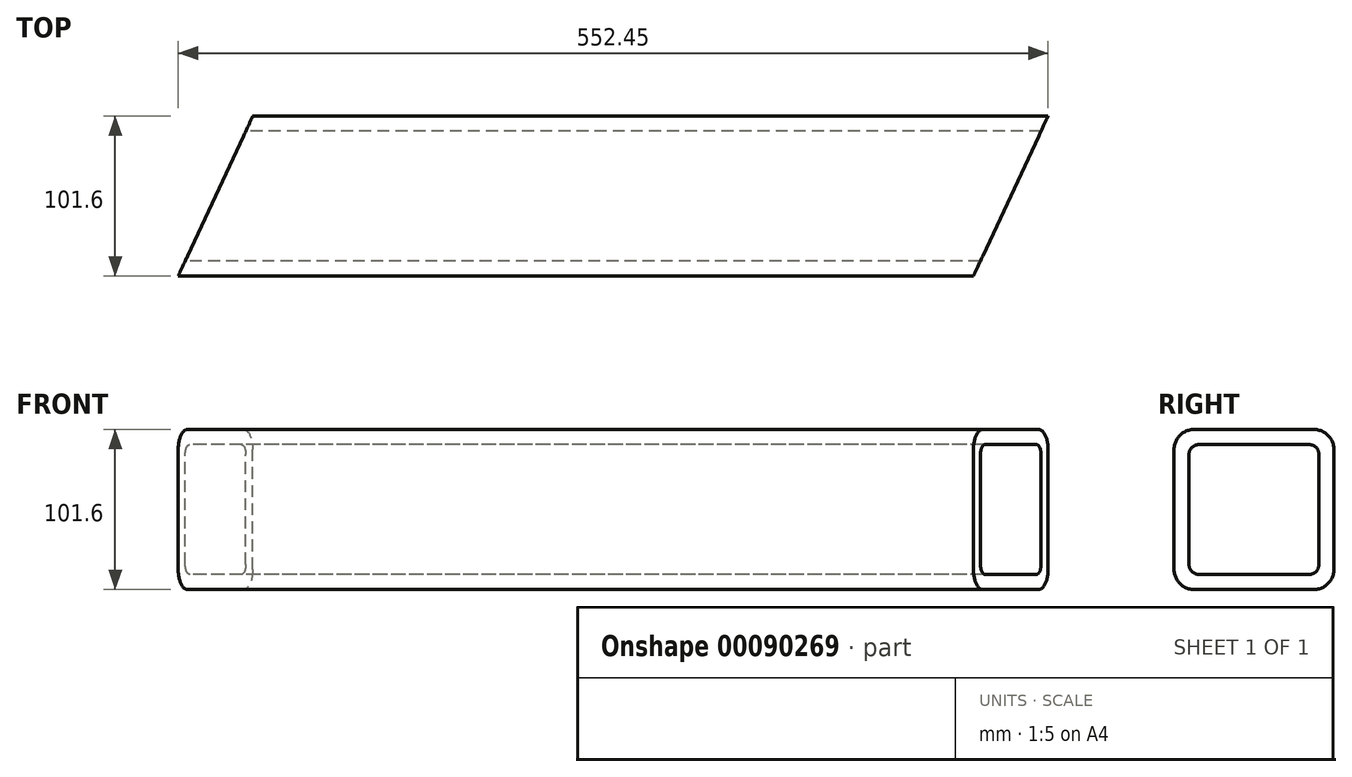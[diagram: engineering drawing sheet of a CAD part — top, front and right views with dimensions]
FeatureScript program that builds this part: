
annotation { "Feature Type Name" : "Feature", "Feature Type Description" : "" }
export const myFeature = defineFeature(function(context is Context, id is Id, definition is map)
    precondition{}
    {
        {
            var Q0;
            Q0=qCreatedBy(makeId("Right.planeOp"),FACE);
            var sketch = newSketch(context, id + "F0", { "sketchPlane" : qUnion([Q0])});
            skLineSegment(sketch, "E0.bottom", {"start": v(12.7, 0) * mm, "end": v(88.9, 0) * mm});
            skLineSegment(sketch, "E0.top", {"start": v(12.7, -101.6) * mm, "end": v(88.9, -101.6) * mm});
            skLineSegment(sketch, "E0.left", {"start": v(0, -12.7) * mm, "end": v(0, -88.9) * mm});
            skLineSegment(sketch, "E0.right", {"start": v(101.6, -12.7) * mm, "end": v(101.6, -88.9) * mm});
            skLineSegment(sketch, "E1.0", {"start": v(15.88, -9.53) * mm, "end": v(85.73, -9.53) * mm});
            skLineSegment(sketch, "E1.1", {"start": v(9.53, -15.88) * mm, "end": v(9.53, -85.73) * mm});
            skLineSegment(sketch, "E1.2", {"start": v(15.88, -92.08) * mm, "end": v(85.73, -92.08) * mm});
            skLineSegment(sketch, "E1.3", {"start": v(92.08, -15.88) * mm, "end": v(92.08, -85.73) * mm});
            skPoint(sketch, "E2.visualSharp", {"position": v(0, 0) * mm});
            skArc(sketch, "E2.filletArc", {"start": v(12.7, 0) * mm, "mid": v(3.72, -3.72) * mm, "end": v(0, -12.7) * mm});
            skPoint(sketch, "E3.visualSharp", {"position": v(101.6, 0) * mm});
            skArc(sketch, "E3.filletArc", {"start": v(101.6, -12.7) * mm, "mid": v(97.88, -3.72) * mm, "end": v(88.9, 0) * mm});
            skPoint(sketch, "E4.visualSharp", {"position": v(101.6, -101.6) * mm});
            skArc(sketch, "E4.filletArc", {"start": v(88.9, -101.6) * mm, "mid": v(97.88, -97.88) * mm, "end": v(101.6, -88.9) * mm});
            skPoint(sketch, "E5.visualSharp", {"position": v(0, -101.6) * mm});
            skArc(sketch, "E5.filletArc", {"start": v(0, -88.9) * mm, "mid": v(3.72, -97.88) * mm, "end": v(12.7, -101.6) * mm});
            skPoint(sketch, "E6.visualSharp", {"position": v(9.53, -92.08) * mm});
            skArc(sketch, "E6.filletArc", {"start": v(9.53, -85.73) * mm, "mid": v(11.38, -90.22) * mm, "end": v(15.88, -92.08) * mm});
            skPoint(sketch, "E7.visualSharp", {"position": v(92.08, -92.08) * mm});
            skArc(sketch, "E7.filletArc", {"start": v(85.73, -92.08) * mm, "mid": v(90.22, -90.22) * mm, "end": v(92.08, -85.73) * mm});
            skPoint(sketch, "E8.visualSharp", {"position": v(92.08, -9.53) * mm});
            skArc(sketch, "E8.filletArc", {"start": v(92.08, -15.88) * mm, "mid": v(90.22, -11.38) * mm, "end": v(85.73, -9.52) * mm});
            skPoint(sketch, "E9.visualSharp", {"position": v(9.53, -9.53) * mm});
            skArc(sketch, "E9.filletArc", {"start": v(15.88, -9.53) * mm, "mid": v(11.38, -11.38) * mm, "end": v(9.53, -15.88) * mm});
            skSolve(sketch);
        }
        {
            var Q0;
            Q0=makeQuery(id+"F0.imprint","IMPRINT",FACE,{"disambiguationData":[TD([[makeQuery(id+"F0.imprint","IMPRINT",EDGE,{"derivedFrom":sQuery(id+"F0.wireOp",EDGE,"E0.bottom")}),-1.0]])]});
            extrude(context, id + "F1", {"entities" : qUnion([Q0]), "depth" : 1651 * mm});
        }
        {
            var Q0;
            Q0=qCreatedBy(makeId("Top.planeOp"),FACE);
            var sketch = newSketch(context, id + "F2", { "sketchPlane" : qUnion([Q0])});
            skLineSegment(sketch, "E10.0", {"start": v(1651, 0) * mm, "end": v(0, 0) * mm});
            skLineSegment(sketch, "E10.1", {"start": v(1651, 101.6) * mm, "end": v(0, 101.6) * mm});
            skLineSegment(sketch, "E11", {"start": v(47.38, 101.6) * mm, "end": v(0, 0) * mm});
            skLineSegment(sketch, "E12", {"start": v(505.07, 0) * mm, "end": v(552.45, 101.6) * mm});
            skLineSegment(sketch, "E13.0", {"start": v(0, 12.7) * mm, "end": v(0, 88.9) * mm});
            skLineSegment(sketch, "E14.0", {"start": v(0, 101.6) * mm, "end": v(0, 88.9) * mm});
            skLineSegment(sketch, "E15.0", {"start": v(0, 12.7) * mm, "end": v(0, 0) * mm});
            skLineSegment(sketch, "E16.0", {"start": v(1651, 12.7) * mm, "end": v(1651, 88.9) * mm});
            skLineSegment(sketch, "E17.0", {"start": v(1651, 101.6) * mm, "end": v(1651, 88.9) * mm});
            skLineSegment(sketch, "E18.0", {"start": v(1651, 12.7) * mm, "end": v(1651, 0) * mm});
            skSolve(sketch);
        }
        {
            var Q0;
            {var subQ0=sQuery(id+"F2.wireOp",EDGE,"E12");Q0=makeQuery(id+"F2.imprint","IMPRINT",FACE,{"disambiguationData":[TD([[makeQuery(id+"F2.imprint","IMPRINT",EDGE,{"derivedFrom":subQ0}),-1.0]])]});}
            var Q1;
            {var subQ1=sQuery(id+"F2.wireOp",EDGE,"E11");Q1=makeQuery(id+"F2.imprint","IMPRINT",FACE,{"disambiguationData":[TD([[makeQuery(id+"F2.imprint","IMPRINT",EDGE,{"derivedFrom":subQ1}),-1.0]])]});}
            extrude(context, id + "F3", {"entities" : qUnion([Q0, Q1]), "operationType" : NewBodyOperationType.REMOVE, "oppositeDirection" : true, "depth" : 127 * mm});
        }
    });
